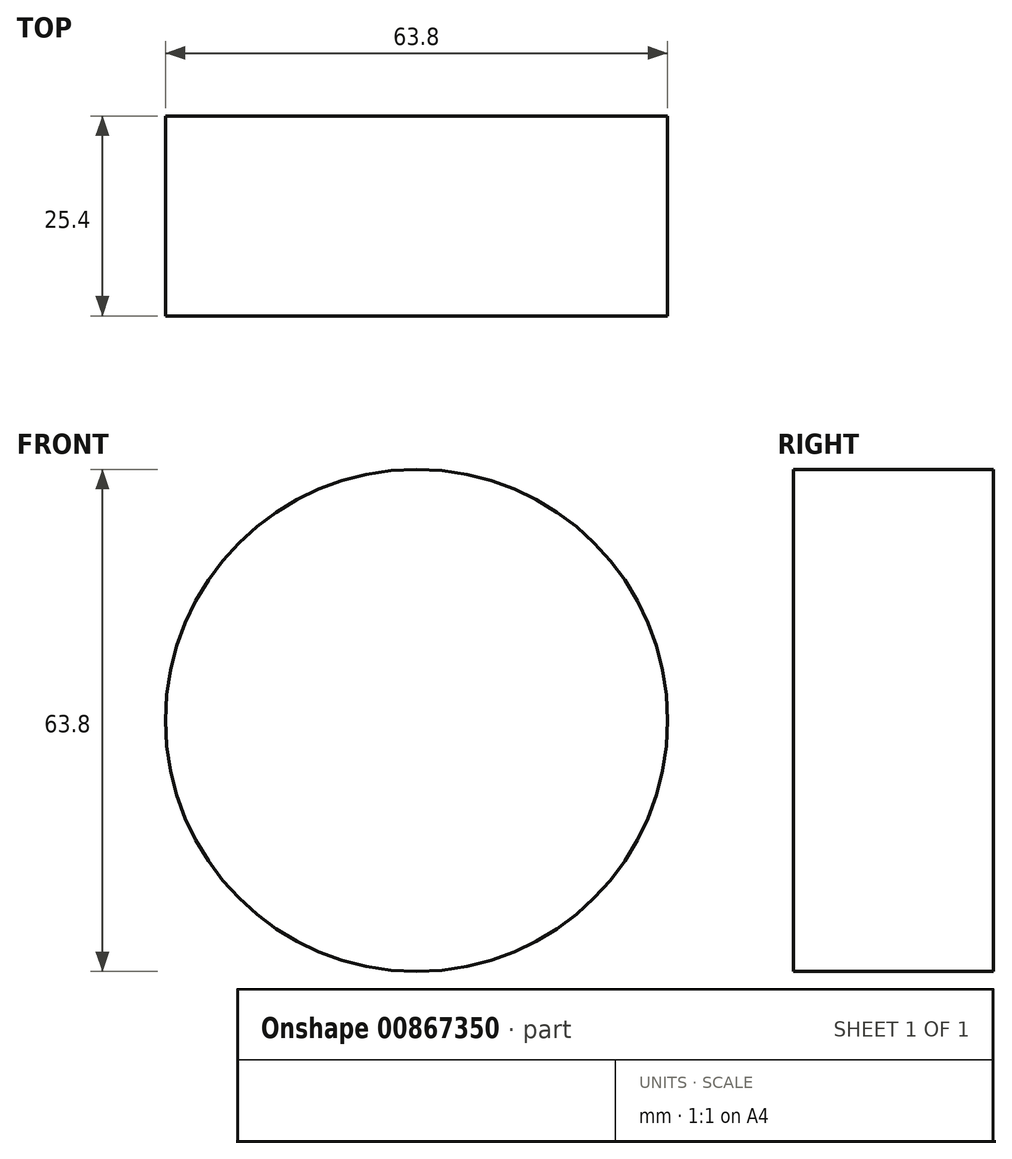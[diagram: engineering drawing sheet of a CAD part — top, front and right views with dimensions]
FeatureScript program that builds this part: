
annotation { "Feature Type Name" : "Feature", "Feature Type Description" : "" }
export const myFeature = defineFeature(function(context is Context, id is Id, definition is map)
    precondition{}
    {
        {
            var Q0;
            Q0=qCreatedBy(makeId("Front.planeOp"),FACE);
            var sketch = newSketch(context, id + "F0", { "sketchPlane" : qUnion([Q0])});
            skCircle(sketch, "E0", {"center": v(0, 0) * mm, "radius": 31.9 * mm});
            skSolve(sketch);
        }
        {
            var Q0;
            Q0 = qSketchRegion(id + "F0", true);
            extrude(context, id + "F1", {"entities" : qUnion([Q0]), "depth" : 25.4 * mm, "offsetDistance" : 25.4 * mm});
        }
    });
